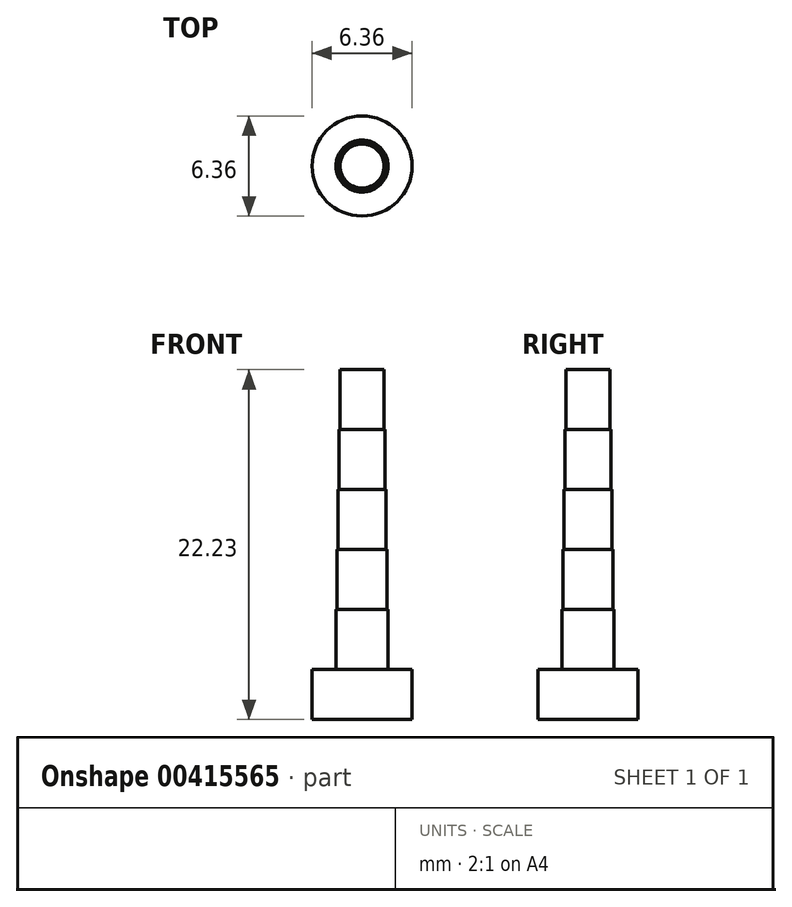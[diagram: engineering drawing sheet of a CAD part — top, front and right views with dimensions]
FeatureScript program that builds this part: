
annotation { "Feature Type Name" : "Feature", "Feature Type Description" : "" }
export const myFeature = defineFeature(function(context is Context, id is Id, definition is map)
    precondition{}
    {
        {
            var Q0;
            Q0=qCreatedBy(makeId("Front.planeOp"),FACE);
            var sketch = newSketch(context, id + "F0", { "sketchPlane" : qUnion([Q0])});
            skLineSegment(sketch, "E0", {"start": v(0, 0) * mm, "end": v(-3.18, 0) * mm});
            skLineSegment(sketch, "E1", {"start": v(-3.18, 3.18) * mm, "end": v(-1.65, 3.18) * mm});
            skLineSegment(sketch, "E2", {"start": v(-1.4, 22.23) * mm, "end": v(0, 22.23) * mm});
            skLineSegment(sketch, "E3", {"start": v(0, 22.23) * mm, "end": v(0, 0) * mm});
            skLineSegment(sketch, "E4", {"start": v(-3.18, 3.18) * mm, "end": v(-3.18, 0) * mm});
            skLineSegment(sketch, "E5.0", {"start": v(-1.46, 18.41) * mm, "end": v(-1.4, 18.41) * mm});
            skLineSegment(sketch, "E6.0", {"start": v(-1.52, 14.6) * mm, "end": v(-1.46, 14.6) * mm});
            skLineSegment(sketch, "E7.0", {"start": v(-1.59, 10.8) * mm, "end": v(0, 10.8) * mm});
            skLineSegment(sketch, "E8.0", {"start": v(-1.65, 6.98) * mm, "end": v(0, 6.98) * mm});
            skLineSegment(sketch, "E9.0", {"start": v(-1.46, 14.6) * mm, "end": v(-1.46, 18.41) * mm});
            skLineSegment(sketch, "E10.trimOffspring", {"start": v(-1.4, 18.41) * mm, "end": v(-1.4, 22.23) * mm});
            skLineSegment(sketch, "E11.0", {"start": v(-1.52, 10.8) * mm, "end": v(-1.52, 14.6) * mm});
            skLineSegment(sketch, "E12.0", {"start": v(-1.59, 6.98) * mm, "end": v(-1.59, 10.8) * mm});
            skLineSegment(sketch, "E13.0", {"start": v(-1.65, 3.18) * mm, "end": v(-1.65, 6.98) * mm});
            skPoint(sketch, "E14.orphan", {"position": v(-1.4, 3.18) * mm});
            skSolve(sketch);
        }
        {
            var Q0;
            {var subQ3=sQuery(id+"F0.wireOp",EDGE,"E12.0");Q0=makeQuery(id+"F0.imprint","IMPRINT",FACE,{"disambiguationData":[TD([[makeQuery(id+"F0.imprint","IMPRINT",EDGE,{"derivedFrom":subQ3}),-1.0]])]});}
            var Q1;
            {var subQ5=sQuery(id+"F0.wireOp",EDGE,"E0");Q1=makeQuery(id+"F0.imprint","IMPRINT",FACE,{"disambiguationData":[TD([[makeQuery(id+"F0.imprint","IMPRINT",EDGE,{"derivedFrom":subQ5}),-1.0]])]});}
            var Q2;
            {var subQ1=sQuery(id+"F0.wireOp",EDGE,"E2");Q2=makeQuery(id+"F0.imprint","IMPRINT",FACE,{"disambiguationData":[TD([[makeQuery(id+"F0.imprint","IMPRINT",EDGE,{"derivedFrom":subQ1}),-1.0]])]});}
            var Q3;
            Q3=sQuery(id+"F0.wireOp",EDGE,"E3");
            revolve(context, id + "F1", {"entities" : qUnion([Q0, Q1, Q2]), "axis" : qUnion([Q3]), "revolveType" : RevolveType.FULL});
        }
    });
